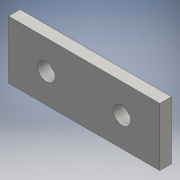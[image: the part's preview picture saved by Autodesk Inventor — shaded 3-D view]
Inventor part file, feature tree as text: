
AUTODESK INVENTOR PART (.ipt)
format: ipt  version: 2016 (Build 200138000, 138)  size: 92,160 bytes
history: native  units: mm
features: extrude x1, sketch x1
ambient origin geometry x8: Origin, YZ Plane, XZ Plane, XY Plane, X Axis, Y Axis, Z Axis, Center Point
bodies: Solid1 (feature_tree)
feature tree (2):
  extrude  "Extrusion1"  Depth=26.0mm
  sketch  "Sketch1"  dims[d0=10.0mm d1=26.0mm d2=3.0mm d4=6.5mm d5=6.5mm d6=13.0mm d7=2.0mm d8=0.0mm]
